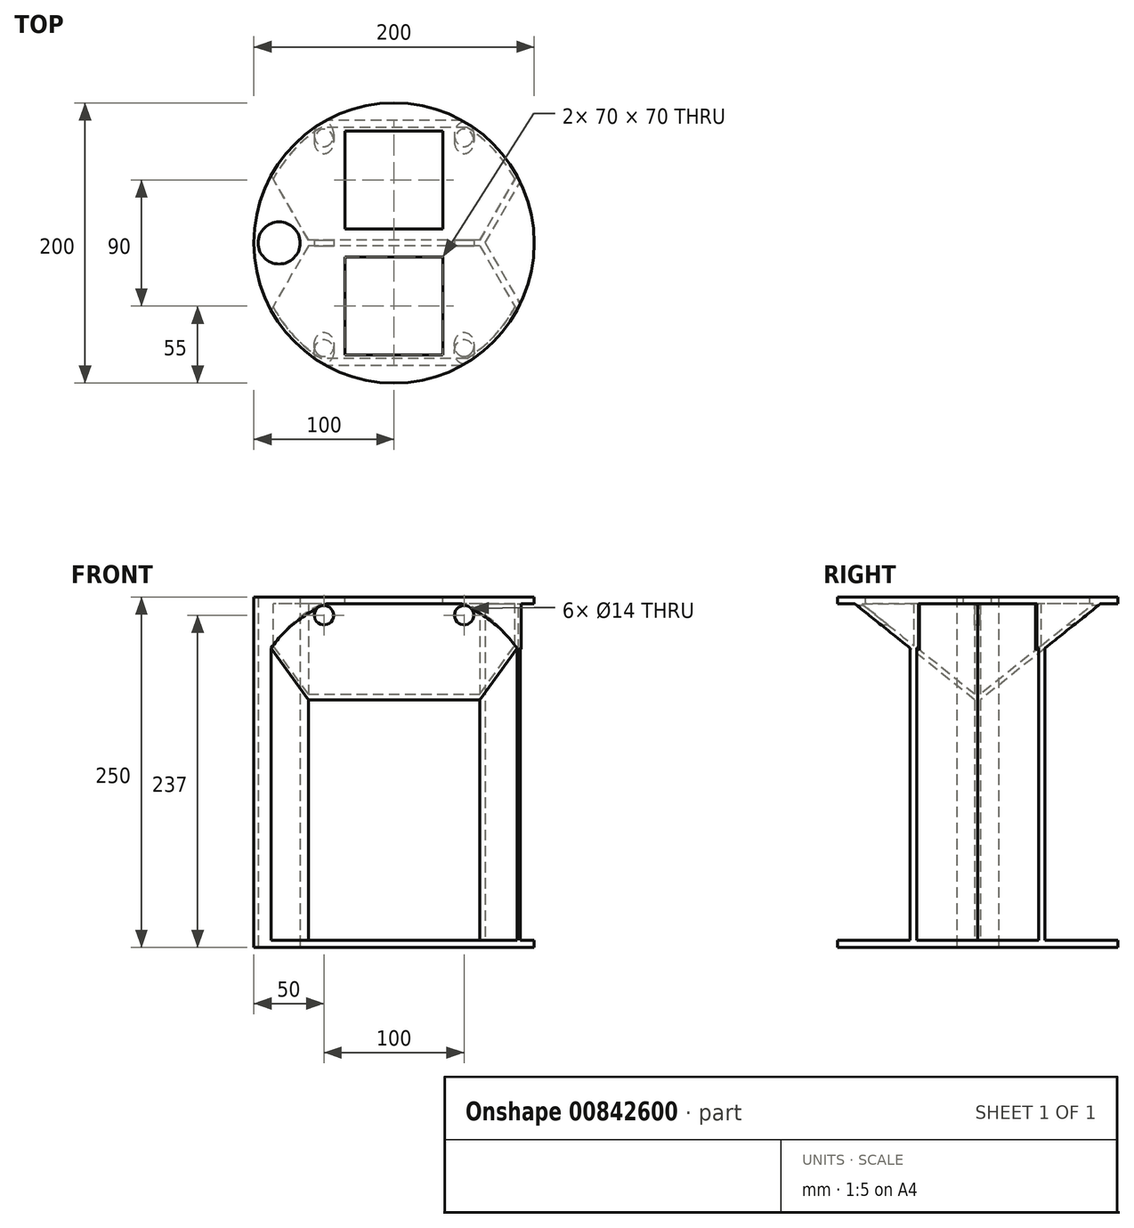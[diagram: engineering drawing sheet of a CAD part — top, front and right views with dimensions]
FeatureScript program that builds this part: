
annotation { "Feature Type Name" : "Feature", "Feature Type Description" : "" }
export const myFeature = defineFeature(function(context is Context, id is Id, definition is map)
    precondition{}
    {
        {
            var Q0;
            Q0=qCreatedBy(makeId("Top.planeOp"),FACE);
            var sketch = newSketch(context, id + "F0", { "sketchPlane" : qUnion([Q0])});
            skCircle(sketch, "E0", {"center": v(0, 0) * mm, "radius": 100 * mm});
            skSolve(sketch);
        }
        {
            var Q0;
            Q0 = qSketchRegion(id + "F0", true);
            extrude(context, id + "F1", {"entities" : qUnion([Q0]), "depth" : 250 * mm, "offsetDistance" : 25 * mm});
        }
        {
            var Q0;
            Q0=qCreatedBy(makeId("Top.planeOp"),FACE);
            var sketch = newSketch(context, id + "F2", { "sketchPlane" : qUnion([Q0])});
            skLineSegment(sketch, "E1", {"start": v(-61.15, 2) * mm, "end": v(-87.72, 48.01) * mm});
            skLineSegment(sketch, "E2", {"start": v(-61.15, -2) * mm, "end": v(-87.72, -48.01) * mm});
            skLineSegment(sketch, "E3", {"start": v(61.15, 2) * mm, "end": v(87.72, 48.01) * mm});
            skLineSegment(sketch, "E4", {"start": v(61.15, -2) * mm, "end": v(87.72, -48.01) * mm});
            skArc(sketch, "E5", {"start": v(-87.72, -48.01) * mm, "mid": v(0, -100) * mm, "end": v(87.72, -48.01) * mm});
            skPoint(sketch, "E6.orphan", {"position": v(-101.03, 0) * mm});
            skArc(sketch, "E7.trimOffspring", {"start": v(87.72, 48.01) * mm, "mid": v(0, 100) * mm, "end": v(-87.72, 48.01) * mm});
            skLineSegment(sketch, "E8.bottom", {"start": v(61.15, 2) * mm, "end": v(-61.15, 2) * mm});
            skLineSegment(sketch, "E8.top", {"start": v(61.15, -2) * mm, "end": v(-61.15, -2) * mm});
            skPoint(sketch, "E9.orphan", {"position": v(-75, 2) * mm});
            skPoint(sketch, "E10.orphan", {"position": v(-75, -2) * mm});
            skPoint(sketch, "E11.orphan", {"position": v(-60, 0) * mm});
            skPoint(sketch, "E8.left.start.orphan", {"position": v(75, 2) * mm});
            skPoint(sketch, "E12.orphan", {"position": v(75, -2) * mm});
            skPoint(sketch, "E13.end.orphan", {"position": v(60, 0) * mm});
            skLineSegment(sketch, "E14", {"start": v(65, 0) * mm, "end": v(90.08, 43.43) * mm});
            skLineSegment(sketch, "E15", {"start": v(65, 0) * mm, "end": v(90.08, -43.43) * mm});
            skArc(sketch, "E16", {"start": v(90.08, -43.43) * mm, "mid": v(100, 0) * mm, "end": v(90.08, 43.43) * mm});
            skSolve(sketch);
        }
        {
            var Q0;
            Q0 = qSketchRegion(id + "F2", true);
            extrude(context, id + "F3", {"entities" : qUnion([Q0]), "operationType" : NewBodyOperationType.REMOVE, "depth" : 245 * mm, "offsetDistance" : 25 * mm});
        }
        {
            var Q0;
            Q0=qCreatedBy(makeId("Top.planeOp"),FACE);
            var sketch = newSketch(context, id + "F4", { "sketchPlane" : qUnion([Q0])});
            skCircle(sketch, "E17", {"center": v(0, 0) * mm, "radius": 100 * mm});
            skSolve(sketch);
        }
        {
            var Q0;
            Q0 = qSketchRegion(id + "F4", true);
            extrude(context, id + "F5", {"entities" : qUnion([Q0]), "operationType" : NewBodyOperationType.ADD, "depth" : 5 * mm, "offsetDistance" : 25 * mm});
        }
        {
            var Q0;
            Q0=makeQuery(id+"F5.boolean.opBoolean","MERGE",FACE,{"derivedFrom":[makeQuery(id+"F1.opExtrude","CAP_FACE",FACE,{"disambiguationData":[OSD([sQuery(id+"F0.wireOp",EDGE,"E0")])],"isStart":true}),makeQuery(id+"F5.opExtrude","CAP_FACE",FACE,{"disambiguationData":[OSD([sQuery(id+"F4.wireOp",EDGE,"E17")])],"isStart":true})]});
            var sketch = newSketch(context, id + "F6", { "sketchPlane" : qUnion([Q0])});
            skCircle(sketch, "E18", {"center": v(-82, 0) * mm, "radius": 15 * mm});
            skSolve(sketch);
        }
        {
            var Q0;
            Q0 = qSketchRegion(id + "F6", true);
            extrude(context, id + "F7", {"entities" : qUnion([Q0]), "operationType" : NewBodyOperationType.REMOVE, "endBound" : BoundingType.THROUGH_ALL, "oppositeDirection" : true, "depth" : 25 * mm, "offsetDistance" : 25 * mm});
        }
        {
            var Q0;
            Q0=qCreatedBy(makeId("Right.planeOp"),FACE);
            var sketch = newSketch(context, id + "F8", { "sketchPlane" : qUnion([Q0])});
            skPoint(sketch, "E19.middle", {"position": v(0, 210) * mm});
            skLineSegment(sketch, "E20", {"start": v(0, 175) * mm, "end": v(-87.5, 245) * mm});
            skPoint(sketch, "E21.orphan", {"position": v(-87.5, 175) * mm});
            skPoint(sketch, "E19.top.start.orphan", {"position": v(87.5, 175) * mm});
            skLineSegment(sketch, "E22", {"start": v(0, 179) * mm, "end": v(-82.5, 245) * mm});
            skPoint(sketch, "E23.start.orphan", {"position": v(0, 245) * mm});
            skLineSegment(sketch, "E24.trimOffspring", {"start": v(-82.5, 245) * mm, "end": v(-87.5, 245) * mm});
            skLineSegment(sketch, "E25", {"start": v(0, 179) * mm, "end": v(0, 175) * mm});
            skPoint(sketch, "E19.bottom.end.orphan", {"position": v(82.5, 245) * mm});
            skPoint(sketch, "E19.bottom.start.orphan", {"position": v(87.5, 245) * mm});
            skSolve(sketch);
        }
        {
            var Q0;
            Q0=qCreatedBy(makeId("Right.planeOp"),FACE);
            var sketch = newSketch(context, id + "F9", { "sketchPlane" : qUnion([Q0])});
            skLineSegment(sketch, "E26.bottom", {"start": v(87.5, 245) * mm, "end": v(82.5, 245) * mm});
            skPoint(sketch, "E26.middle", {"position": v(0, 210) * mm});
            skLineSegment(sketch, "E27", {"start": v(0, 175) * mm, "end": v(87.5, 245) * mm});
            skPoint(sketch, "E28.orphan", {"position": v(-87.5, 175) * mm});
            skPoint(sketch, "E26.top.start.orphan", {"position": v(87.5, 175) * mm});
            skLineSegment(sketch, "E29", {"start": v(0, 179) * mm, "end": v(82.5, 245) * mm});
            skPoint(sketch, "E30.start.orphan", {"position": v(0, 245) * mm});
            skLineSegment(sketch, "E31", {"start": v(0, 179) * mm, "end": v(0, 175) * mm});
            skPoint(sketch, "E32.trimOffspring.end.orphan", {"position": v(-87.5, 245) * mm});
            skPoint(sketch, "E32.trimOffspring.start.orphan", {"position": v(-82.5, 245) * mm});
            skSolve(sketch);
        }
        {
            var Q0;
            Q0 = qSketchRegion(id + "F8", true);
            var Q1;
            Q1=makeQuery(id+"F3.boolean.opBoolean","COPY",FACE,{"derivedFrom":makeQuery(id+"F3.opExtrude","SWEPT_FACE",FACE,{"disambiguationData":[OSD([sQuery(id+"F2.wireOp",EDGE,"E4")])]})});
            var Q2;
            Q2=makeQuery(id+"F3.boolean.opBoolean","COPY",FACE,{"derivedFrom":makeQuery(id+"F3.opExtrude","SWEPT_FACE",FACE,{"disambiguationData":[OSD([sQuery(id+"F2.wireOp",EDGE,"E2")])]})});
            extrude(context, id + "F10", {"entities" : qUnion([Q0]), "operationType" : NewBodyOperationType.ADD, "endBound" : BoundingType.UP_TO_SURFACE, "depth" : 25 * mm, "endBoundEntityFace" : qUnion([Q1]), "offsetDistance" : 25 * mm, "hasSecondDirection" : true, "secondDirectionBound" : SecondDirectionBoundingType.UP_TO_SURFACE, "secondDirectionOppositeDirection" : true, "secondDirectionDepth" : 25 * mm, "secondDirectionBoundEntityFace" : qUnion([Q2])});
        }
        {
            var Q0;
            Q0 = qSketchRegion(id + "F9", true);
            var Q1;
            Q1=makeQuery(id+"F3.boolean.opBoolean","COPY",FACE,{"derivedFrom":makeQuery(id+"F3.opExtrude","SWEPT_FACE",FACE,{"disambiguationData":[OSD([sQuery(id+"F2.wireOp",EDGE,"E3")])]})});
            var Q2;
            Q2=makeQuery(id+"F3.boolean.opBoolean","COPY",FACE,{"derivedFrom":makeQuery(id+"F3.opExtrude","SWEPT_FACE",FACE,{"disambiguationData":[OSD([sQuery(id+"F2.wireOp",EDGE,"E1")])]})});
            extrude(context, id + "F11", {"entities" : qUnion([Q0]), "operationType" : NewBodyOperationType.ADD, "endBound" : BoundingType.UP_TO_SURFACE, "depth" : 25 * mm, "endBoundEntityFace" : qUnion([Q1]), "offsetDistance" : 25 * mm, "hasSecondDirection" : true, "secondDirectionBound" : SecondDirectionBoundingType.UP_TO_SURFACE, "secondDirectionOppositeDirection" : true, "secondDirectionDepth" : 25 * mm, "secondDirectionBoundEntityFace" : qUnion([Q2])});
        }
        {
            var Q0;
            Q0=qCreatedBy(makeId("Top.planeOp"),FACE);
            var sketch = newSketch(context, id + "F12", { "sketchPlane" : qUnion([Q0])});
            skCircle(sketch, "E33", {"center": v(0, 0) * mm, "radius": 100 * mm});
            skCircle(sketch, "E34", {"center": v(0, 0) * mm, "radius": 200 * mm});
            skSolve(sketch);
        }
        {
            var Q0;
            Q0=makeQuery(id+"F12.imprint","IMPRINT",FACE,{"disambiguationData":[TD([[makeQuery(id+"F12.imprint","IMPRINT",EDGE,{"derivedFrom":sQuery(id+"F12.wireOp",EDGE,"E33")}),-1.0]])]});
            extrude(context, id + "F13", {"entities" : qUnion([Q0]), "operationType" : NewBodyOperationType.REMOVE, "endBound" : BoundingType.THROUGH_ALL, "depth" : 25 * mm, "offsetDistance" : 25 * mm});
        }
        {
            var Q0;
            Q0=makeQuery(id+"F1.opExtrude","CAP_FACE",FACE,{"disambiguationData":[OSD([sQuery(id+"F0.wireOp",EDGE,"E0")])],"isStart":false});
            var sketch = newSketch(context, id + "F14", { "sketchPlane" : qUnion([Q0])});
            skLineSegment(sketch, "E35.bottom", {"start": v(35, 80) * mm, "end": v(-35, 80) * mm});
            skLineSegment(sketch, "E35.top", {"start": v(35, 10) * mm, "end": v(-35, 10) * mm});
            skLineSegment(sketch, "E35.left", {"start": v(35, 80) * mm, "end": v(35, 10) * mm});
            skLineSegment(sketch, "E35.right", {"start": v(-35, 80) * mm, "end": v(-35, 10) * mm});
            skPoint(sketch, "E35.middle", {"position": v(0, 45) * mm});
            skLineSegment(sketch, "E36.bottom", {"start": v(35, -10) * mm, "end": v(-35, -10) * mm});
            skLineSegment(sketch, "E36.top", {"start": v(35, -80) * mm, "end": v(-35, -80) * mm});
            skLineSegment(sketch, "E36.left", {"start": v(35, -10) * mm, "end": v(35, -80) * mm});
            skLineSegment(sketch, "E36.right", {"start": v(-35, -10) * mm, "end": v(-35, -80) * mm});
            skPoint(sketch, "E36.middle", {"position": v(0, -45) * mm});
            skSolve(sketch);
        }
        {
            var Q0;
            Q0 = qSketchRegion(id + "F14", true);
            extrude(context, id + "F15", {"entities" : qUnion([Q0]), "operationType" : NewBodyOperationType.REMOVE, "oppositeDirection" : true, "depth" : 5 * mm, "offsetDistance" : 25 * mm});
        }
        {
            var Q0;
            {var subQ0=sQuery(id+"F2.wireOp",EDGE,"E4");var subQ1=sQuery(id+"F2.wireOp",EDGE,"E8.top");var subQ2=sQuery(id+"F2.wireOp",EDGE,"E2");Q0=makeQuery(id+"F10.boolean.opBoolean","SPLIT",FACE,{"disambiguationData":[TD([makeQuery(id+"F3.boolean.opBoolean","COPY",FACE,{"derivedFrom":makeQuery(id+"F3.opExtrude","SWEPT_FACE",FACE,{"disambiguationData":[OSD([subQ2])]})})])],"derivedFrom":makeQuery(id+"F3.boolean.opBoolean","COPY",FACE,{"derivedFrom":makeQuery(id+"F3.opExtrude","CAP_FACE",FACE,{"disambiguationData":[OSD([subQ2,subQ0,sQuery(id+"F2.wireOp",EDGE,"E5"),subQ1])],"isStart":false})})});}
            var sketch = newSketch(context, id + "F16", { "sketchPlane" : qUnion([Q0])});
            skArc(sketch, "E37", {"start": v(-90.63, -42.26) * mm, "mid": v(-75.98, -65.01) * mm, "end": v(-55.78, -83) * mm});
            skArc(sketch, "E38", {"start": v(-88.37, -41.2) * mm, "mid": v(-72.82, -64.83) * mm, "end": v(-51.16, -83) * mm});
            skLineSegment(sketch, "E39", {"start": v(-88.37, -41.2) * mm, "end": v(-90.63, -42.26) * mm});
            skLineSegment(sketch, "E40", {"start": v(88.37, -41.2) * mm, "end": v(90.63, -42.26) * mm});
            skLineSegment(sketch, "E41", {"start": v(-55.78, -83) * mm, "end": v(-51.16, -83) * mm});
            skArc(sketch, "E42.trimOffspring", {"start": v(55.78, -83) * mm, "mid": v(75.98, -65.01) * mm, "end": v(90.63, -42.26) * mm});
            skArc(sketch, "E43.trimOffspring", {"start": v(51.16, -83) * mm, "mid": v(72.82, -64.83) * mm, "end": v(88.37, -41.2) * mm});
            skLineSegment(sketch, "E44.trimOffspring", {"start": v(51.16, -83) * mm, "end": v(55.78, -83) * mm});
            skPoint(sketch, "E45.orphan", {"position": v(90.63, -83) * mm});
            skSolve(sketch);
        }
        {
            var Q0;
            Q0 = qSketchRegion(id + "F16", true);
            var Q1;
            Q1=makeQuery(id+"F11.opExtrude","SWEPT_FACE",FACE,{"disambiguationData":[OSD([sQuery(id+"F9.wireOp",EDGE,"E29")])]});
            extrude(context, id + "F17", {"entities" : qUnion([Q0]), "operationType" : NewBodyOperationType.ADD, "endBound" : BoundingType.UP_TO_SURFACE, "depth" : 25 * mm, "endBoundEntityFace" : qUnion([Q1]), "offsetDistance" : 25 * mm});
        }
        {
            var Q0;
            {var subQ0=sQuery(id+"F2.wireOp",EDGE,"E4");var subQ1=sQuery(id+"F2.wireOp",EDGE,"E8.top");var subQ2=sQuery(id+"F2.wireOp",EDGE,"E2");Q0=makeQuery(id+"F10.boolean.opBoolean","SPLIT",FACE,{"disambiguationData":[TD([makeQuery(id+"F3.boolean.opBoolean","COPY",FACE,{"derivedFrom":makeQuery(id+"F3.opExtrude","SWEPT_FACE",FACE,{"disambiguationData":[OSD([subQ2])]})})])],"derivedFrom":makeQuery(id+"F3.boolean.opBoolean","COPY",FACE,{"derivedFrom":makeQuery(id+"F3.opExtrude","CAP_FACE",FACE,{"disambiguationData":[OSD([subQ2,subQ0,sQuery(id+"F2.wireOp",EDGE,"E5"),subQ1])],"isStart":false})})});}
            var sketch = newSketch(context, id + "F18", { "sketchPlane" : qUnion([Q0])});
            skArc(sketch, "E46", {"start": v(90.63, 42.26) * mm, "mid": v(75.98, 65.01) * mm, "end": v(55.78, 83) * mm});
            skArc(sketch, "E47", {"start": v(88.37, 41.2) * mm, "mid": v(72.82, 64.83) * mm, "end": v(51.16, 83) * mm});
            skLineSegment(sketch, "E48", {"start": v(88.37, 41.2) * mm, "end": v(90.63, 42.26) * mm});
            skLineSegment(sketch, "E49", {"start": v(-88.37, 41.2) * mm, "end": v(-90.63, 42.26) * mm});
            skLineSegment(sketch, "E50", {"start": v(-55.78, 83) * mm, "end": v(-51.16, 83) * mm});
            skArc(sketch, "E51.trimOffspring", {"start": v(-51.16, 83) * mm, "mid": v(-72.82, 64.83) * mm, "end": v(-88.37, 41.2) * mm});
            skArc(sketch, "E52.trimOffspring", {"start": v(-55.78, 83) * mm, "mid": v(-75.98, 65.01) * mm, "end": v(-90.63, 42.26) * mm});
            skLineSegment(sketch, "E53.trimOffspring", {"start": v(51.16, 83) * mm, "end": v(55.78, 83) * mm});
            skSolve(sketch);
        }
        {
            var Q0;
            Q0 = qSketchRegion(id + "F18", true);
            var Q1;
            Q1=makeQuery(id+"F10.opExtrude","SWEPT_FACE",FACE,{"disambiguationData":[OSD([sQuery(id+"F8.wireOp",EDGE,"E22")])]});
            extrude(context, id + "F19", {"entities" : qUnion([Q0]), "operationType" : NewBodyOperationType.ADD, "endBound" : BoundingType.UP_TO_SURFACE, "depth" : 25 * mm, "endBoundEntityFace" : qUnion([Q1]), "offsetDistance" : 25 * mm});
        }
        {
            var Q0;
            Q0=qCreatedBy(makeId("Front.planeOp"),FACE);
            cPlane(context, id + "F20", {"entities" : qUnion([Q0]), "cplaneType" : CPlaneType.OFFSET, "offset" : 150 * mm, "width" : 150 * mm, "height" : 150 * mm});
        }
        {
            var Q0;
            Q0=qCreatedBy(id+"F20.planeOp",FACE);
            var sketch = newSketch(context, id + "F21", { "sketchPlane" : qUnion([Q0])});
            skCircle(sketch, "E54", {"center": v(-50, 237) * mm, "radius": 7 * mm});
            skCircle(sketch, "E55", {"center": v(50, 237) * mm, "radius": 7 * mm});
            skSolve(sketch);
        }
        {
            var Q0;
            Q0 = qSketchRegion(id + "F21", true);
            extrude(context, id + "F22", {"entities" : qUnion([Q0]), "operationType" : NewBodyOperationType.REMOVE, "endBound" : BoundingType.THROUGH_ALL, "oppositeDirection" : true, "depth" : 155 * mm, "offsetDistance" : 25 * mm});
        }
    });
